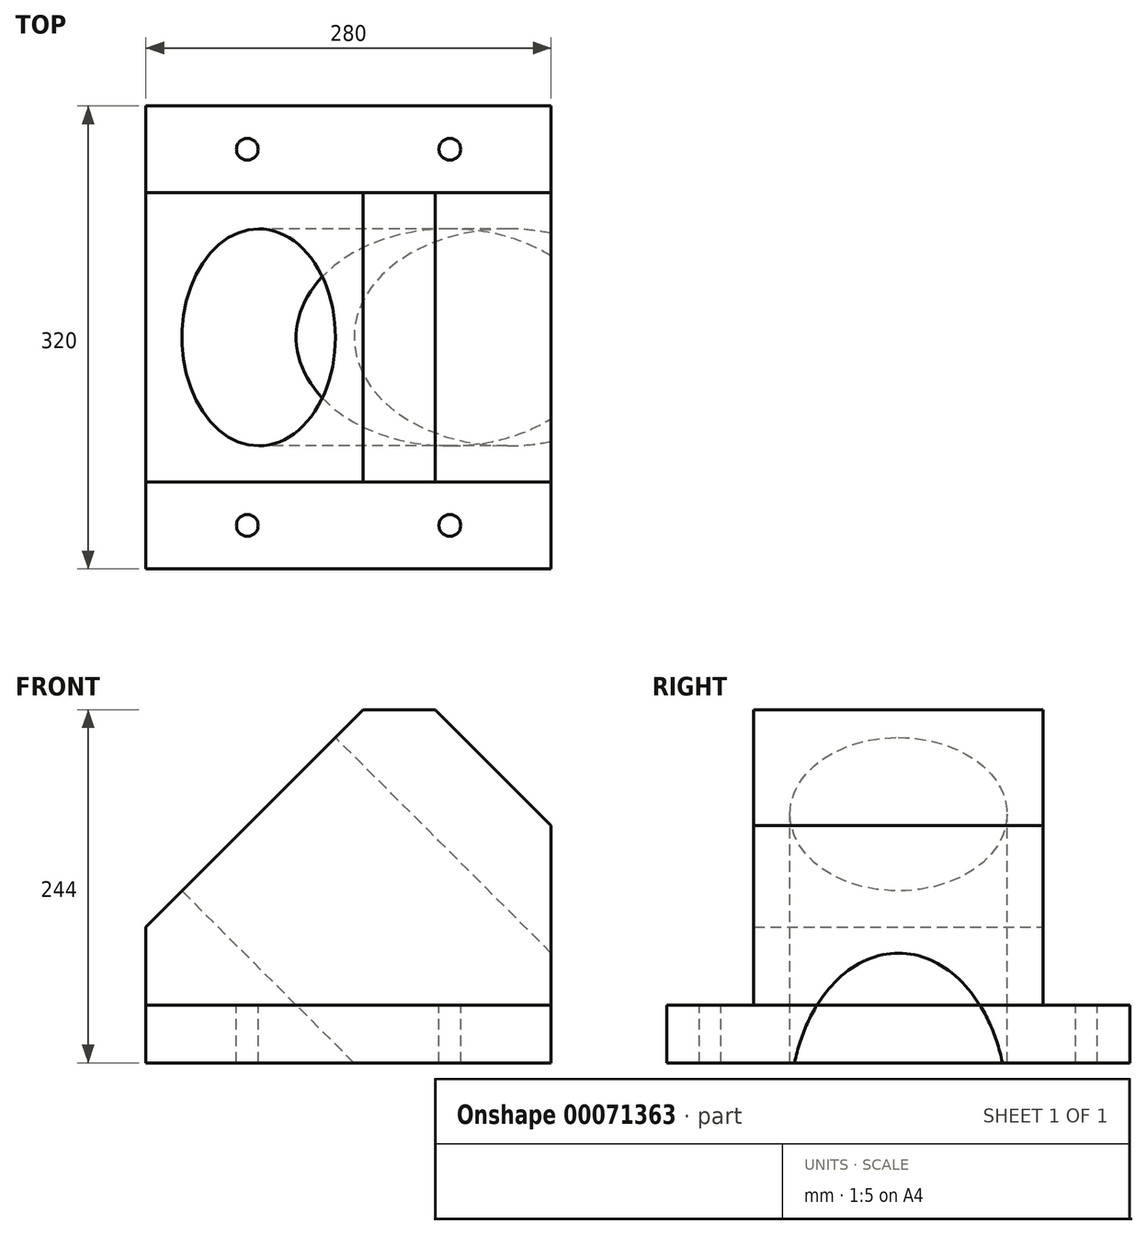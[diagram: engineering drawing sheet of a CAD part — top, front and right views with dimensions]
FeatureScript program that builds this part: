
annotation { "Feature Type Name" : "Feature", "Feature Type Description" : "" }
export const myFeature = defineFeature(function(context is Context, id is Id, definition is map)
    precondition{}
    {
        {
            var Q0;
            Q0=qCreatedBy(makeId("Front.planeOp"),FACE);
            var sketch = newSketch(context, id + "F0", { "sketchPlane" : qUnion([Q0])});
            skLineSegment(sketch, "E0.bottom", {"start": v(10, 122) * mm, "end": v(60, 122) * mm});
            skLineSegment(sketch, "E0.top", {"start": v(-140, -122) * mm, "end": v(140, -122) * mm});
            skLineSegment(sketch, "E0.left", {"start": v(-140, -28) * mm, "end": v(-140, -122) * mm});
            skLineSegment(sketch, "E0.right", {"start": v(140, 42) * mm, "end": v(140, -122) * mm});
            skPoint(sketch, "E0.middle", {"position": v(0, 0) * mm});
            skLineSegment(sketch, "E1", {"start": v(-140, -82) * mm, "end": v(140, -82) * mm});
            skLineSegment(sketch, "E2", {"start": v(60, 122) * mm, "end": v(140, 42) * mm});
            skPoint(sketch, "E3.orphan", {"position": v(140, 122) * mm});
            skLineSegment(sketch, "E4", {"start": v(10, 122) * mm, "end": v(-140, -28) * mm});
            skPoint(sketch, "E5.orphan", {"position": v(-140, 122) * mm});
            skSolve(sketch);
        }
        {
            var Q0;
            {var subQ0=sQuery(id+"F0.wireOp",EDGE,"E0.top");Q0=makeQuery(id+"F0.imprint","IMPRINT",FACE,{"disambiguationData":[TD([[makeQuery(id+"F0.imprint","IMPRINT",EDGE,{"derivedFrom":subQ0}),1.0]])]});}
            extrude(context, id + "F1", {"entities" : qUnion([Q0]), "depth" : 320 * mm, "symmetric" : true});
        }
        {
            var Q0;
            Q0=makeQuery(id+"F0.imprint","IMPRINT",FACE,{"disambiguationData":[TD([[makeQuery(id+"F0.imprint","IMPRINT",EDGE,{"derivedFrom":sQuery(id+"F0.wireOp",EDGE,"E0.bottom")}),-1.0]])]});
            extrude(context, id + "F2", {"entities" : qUnion([Q0]), "depth" : 200 * mm, "symmetric" : true});
        }
        {
            var Q0;
            Q0=makeQuery(id+"F2.opExtrude","SWEPT_FACE",FACE,{"disambiguationData":[OSD([sQuery(id+"F0.wireOp",EDGE,"E4")])]});
            var sketch = newSketch(context, id + "F3", { "sketchPlane" : qUnion([Q0])});
            skCircle(sketch, "E6", {"center": v(0, -8.64) * mm, "radius": 75 * mm});
            skSolve(sketch);
        }
        {
            var Q0;
            Q0=makeQuery(id+"F1.opExtrude","SWEPT_FACE",FACE,{"disambiguationData":[OSD([sQuery(id+"F0.wireOp",EDGE,"E1")])]});
            var sketch = newSketch(context, id + "F4", { "sketchPlane" : qUnion([Q0])});
            skCircle(sketch, "E7", {"center": v(70, 130) * mm, "radius": 7.5 * mm});
            skCircle(sketch, "E8", {"center": v(-70, 130) * mm, "radius": 7.5 * mm});
            skSolve(sketch);
        }
        {
            var Q0;
            Q0=makeQuery(id+"F4.imprint","IMPRINT",FACE,{"disambiguationData":[TD([[makeQuery(id+"F4.imprint","IMPRINT",EDGE,{"derivedFrom":sQuery(id+"F4.wireOp",EDGE,"E7")}),-1.0]])]});
            var sketch = newSketch(context, id + "F5", { "sketchPlane" : qUnion([Q0])});
            skCircle(sketch, "E9", {"center": v(70, -130) * mm, "radius": 7.5 * mm});
            skCircle(sketch, "E10", {"center": v(-70, -130) * mm, "radius": 7.5 * mm});
            skSolve(sketch);
        }
        {
            var Q0;
            Q0=makeQuery(id+"F4.imprint","IMPRINT",FACE,{"disambiguationData":[TD([[makeQuery(id+"F4.imprint","IMPRINT",EDGE,{"derivedFrom":sQuery(id+"F4.wireOp",EDGE,"E7")}),1.0]])]});
            var Q1;
            Q1=makeQuery(id+"F4.imprint","IMPRINT",FACE,{"disambiguationData":[TD([[makeQuery(id+"F4.imprint","IMPRINT",EDGE,{"derivedFrom":sQuery(id+"F4.wireOp",EDGE,"E8")}),1.0]])]});
            var Q2;
            Q2=makeQuery(id+"F5.imprint","IMPRINT",FACE,{"disambiguationData":[TD([[makeQuery(id+"F5.imprint","IMPRINT",EDGE,{"derivedFrom":sQuery(id+"F5.wireOp",EDGE,"E10")}),1.0]])]});
            var Q3;
            Q3=makeQuery(id+"F5.imprint","IMPRINT",FACE,{"disambiguationData":[TD([[makeQuery(id+"F5.imprint","IMPRINT",EDGE,{"derivedFrom":sQuery(id+"F5.wireOp",EDGE,"E9")}),1.0]])]});
            extrude(context, id + "F6", {"entities" : qUnion([Q0, Q1, Q2, Q3]), "operationType" : NewBodyOperationType.REMOVE, "endBound" : BoundingType.THROUGH_ALL, "oppositeDirection" : true, "depth" : 25.4 * mm});
        }
        {
            var Q0;
            Q0=makeQuery(id+"F3.imprint","IMPRINT",FACE,{"disambiguationData":[TD([[makeQuery(id+"F3.imprint","IMPRINT",EDGE,{"derivedFrom":sQuery(id+"F3.wireOp",EDGE,"E6")}),1.0]])]});
            extrude(context, id + "F7", {"entities" : qUnion([Q0]), "operationType" : NewBodyOperationType.REMOVE, "endBound" : BoundingType.THROUGH_ALL, "oppositeDirection" : true, "depth" : 25.4 * mm});
        }
    });
